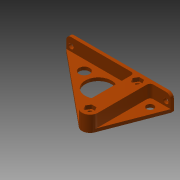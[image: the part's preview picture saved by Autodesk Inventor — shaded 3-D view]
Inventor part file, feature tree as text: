
AUTODESK INVENTOR PART (.ipt)
format: ipt  version: 2013 (Build 170138000, 138)  size: 172,544 bytes
history: native  units: in
note: dims shown in document units (in); Inventor stores cm internally (conversion verified against a paired STEP export)
features: sketch x8, other x3
ambient origin geometry x8: Origin, YZ Plane, XZ Plane, XY Plane, X Axis, Y Axis, Z Axis, Center Point
bodies: Solid1 (feature_tree)
feature tree (11):
  other  "bed bracket right.ipt"
  other  "Solid1::bed bracket right.ipt"
  other  "TaggingFeature1"
  sketch  "Sketch1"  dims[d0=0.3937in]
  sketch  "Sketch2"  dims[d1=2.9528in d2=0.3189in d3=6.4961in d4=0.4921in d5=0.1969in d6=1.7717in d7=0.1969in d8=0.0in d9=0.7874in d10=0.0in d11=0.3189in d13=5.9055in d14=0.2953in d15=0.4921in d17=0.0in d18=0.1969in d19=0.5157in d20=0.2362in d21=0.0in d31=0.2953in d34=0.0in d37=0.2953in d40=0.0in d41=0.2953in d44=0.0in d45=0.2953in d48=0.0in d49=0.2953in]
  sketch  "Sketch3"
  sketch  "Sketch4"
  sketch  "Sketch7"
  sketch  "Sketch8"
  sketch  "Sketch9"
  sketch  "Sketch10"
